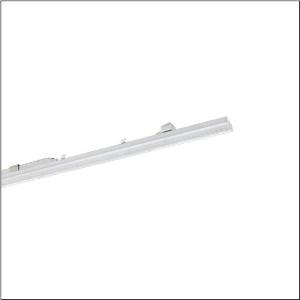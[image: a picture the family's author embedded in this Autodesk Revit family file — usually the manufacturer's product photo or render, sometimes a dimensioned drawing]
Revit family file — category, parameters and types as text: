
# Revit family: tl_l_5wd7a8h0a2b5
name_source: partatom
category: Lighting Fixtures
units: mm (PartAtom-declared; Revit-internal decimal feet)

## family parameters
Cut with Voids When Loaded = No
Host = Face
Light Source = No
Part Type = Normal
Room Calculation Point = No
Round Connector Dimension = Use Diameter
Shared = No

## types (1)
- --- (1 x LED, 850 lm, 4.5 W, 4000K)
    Apparent Load = 5 VA
    CIE Flux Codes = 49 84 98 100 100
    Color Rendering = 80
    Color Temperature = 4000K
    Default Elevation = 1800 mm
    Description = TL L, luminaire insert, of sheet steel, galvanised, coil coated, white, length: 1.500mm, width: 66mm, height: 67mm, LED rated luminous flux: 4.990lm, light colour: 840, control gear: emergency light, with terminal, 3-pole, mains connection: 230..240V, AC, 50/60Hz, rated input power: 34W, primary optical cover: cover, of PMMA, light emission: direct distribution, protection rating (complete): as luminaire, insulation class (complete): insulation class I (protective earthing), certification: CE, impact resistance: IK06, permissible ambient temperature for indoor applications: +5..+35°C, packaging unit: 1 piece
    Height = 120 mm
    Lamp = 1 x LED
    Lamp Light Flux = 850 lm
    Lamp Power = 4.5 W
    Lamp count = 1
    Length = 1690 mm
    Luminous efficacy = 189 lm/W
    Manufacturer = Siteco
    ModVariant = No
    Model = 5WD7A8H0A2B5
    Mounting Place = Ceiling
    Mounting Type = Pendant
    Number of Poles = 1
    OnlyDefault = Yes
    Power Factor = 1
    Product Name = TL L
    Product group = luminaire insert
    ProductGroupID = 901
    Protection Class = Protection class I
    Protection Degree = Degree of protection
    RLX_Detail_Level = 1
    RLX_Emergency_Light_Flux = 0 lm
    RLX_Emergency_Type = 0
    RLX_Emergency_Type_DB = No
    RlxData = <blob elided: 17325 chars, md5=a68cc6b8>
    Socket = socket
    Standby Power = 0 W
    System Light Flux = 850 lm
    System Power = 5 W
    Type Comments = : emergency light operation: 3 h
    Type Image = l_1294382.jpg
    URL = http://relux.com
    VarID = @adj_012053
    Voltage = 0 V
    Weight = 0.00 kg
    Width = 208 mm

## geometry (parser evidence)
native form markers: Blend x4, Sweep x9
no freeform markers — native parametric forms only
